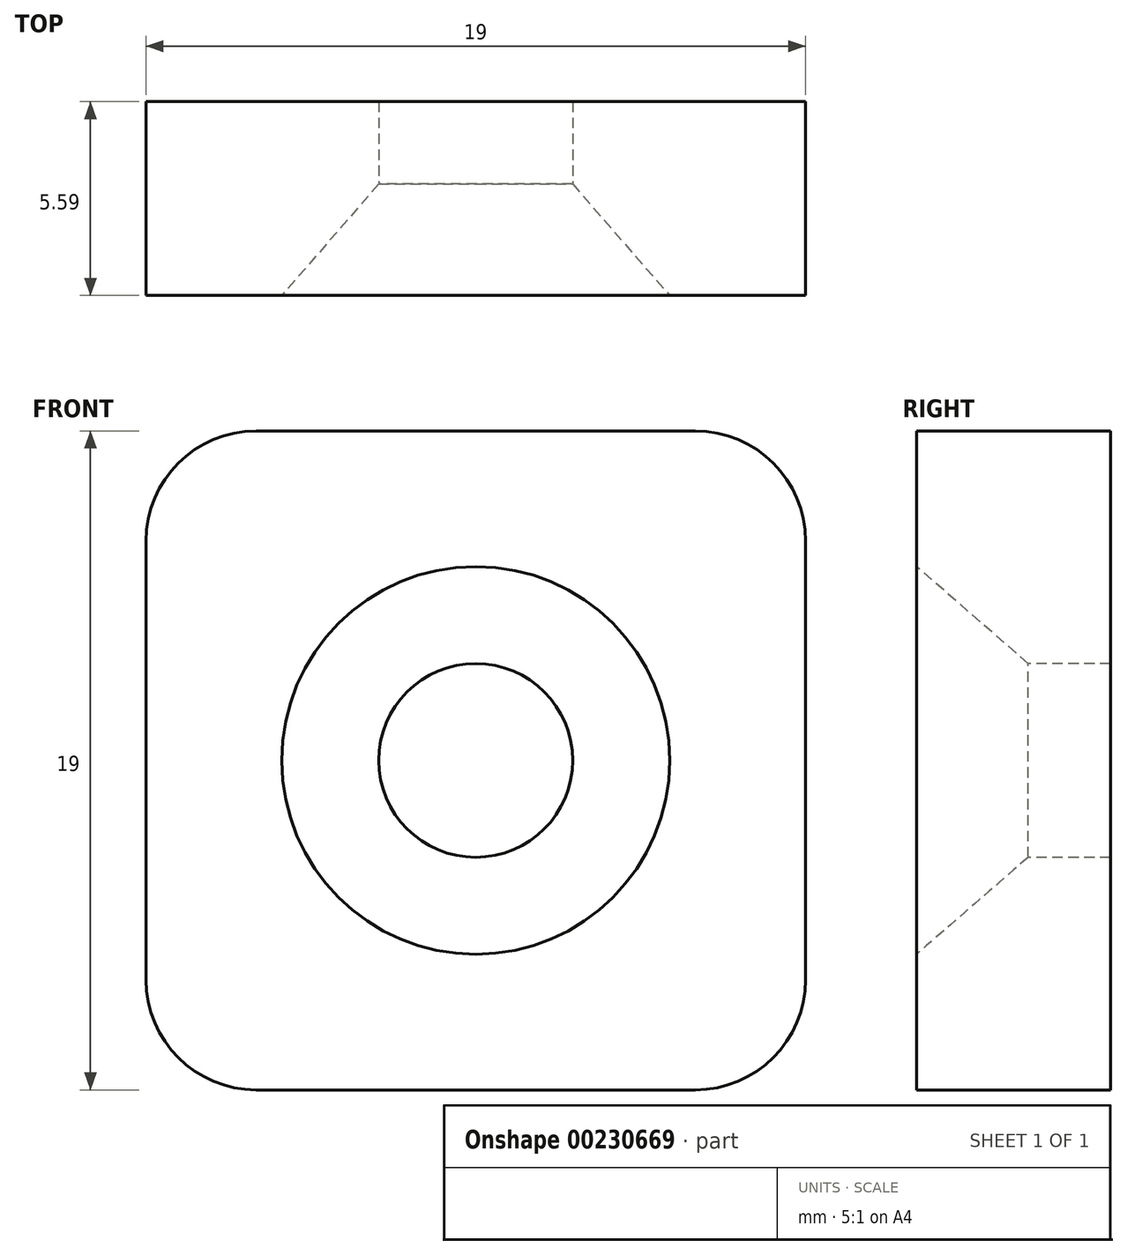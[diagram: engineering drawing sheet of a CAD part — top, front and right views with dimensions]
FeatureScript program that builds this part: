
annotation { "Feature Type Name" : "Feature", "Feature Type Description" : "" }
export const myFeature = defineFeature(function(context is Context, id is Id, definition is map)
    precondition{}
    {
        {
            var Q0;
            Q0=qCreatedBy(makeId("Front.planeOp"),FACE);
            var sketch = newSketch(context, id + "F0", { "sketchPlane" : qUnion([Q0])});
            skLineSegment(sketch, "E0.bottom", {"start": v(0, 0) * mm, "end": v(19, 0) * mm});
            skLineSegment(sketch, "E0.top", {"start": v(0, 19) * mm, "end": v(19, 19) * mm});
            skLineSegment(sketch, "E0.left", {"start": v(0, 0) * mm, "end": v(0, 19) * mm});
            skLineSegment(sketch, "E0.right", {"start": v(19, 0) * mm, "end": v(19, 19) * mm});
            skSolve(sketch);
        }
        {
            var Q0;
            Q0 = qSketchRegion(id + "F0", true);
            extrude(context, id + "F1", {"entities" : qUnion([Q0]), "depth" : 5.6 * mm});
        }
        {
            var Q0;
            Q0=makeQuery(id+"F1.opExtrude","SWEPT_EDGE",EDGE,{"disambiguationData":[OSD([sQuery(id+"F0.wireOp",EDGE,"E0.top"),sQuery(id+"F0.wireOp",EDGE,"E0.left")])]});
            var Q1;
            Q1=makeQuery(id+"F1.opExtrude","SWEPT_EDGE",EDGE,{"disambiguationData":[OSD([sQuery(id+"F0.wireOp",EDGE,"E0.top"),sQuery(id+"F0.wireOp",EDGE,"E0.right")])]});
            var Q2;
            Q2=makeQuery(id+"F1.opExtrude","SWEPT_EDGE",EDGE,{"disambiguationData":[OSD([sQuery(id+"F0.wireOp",EDGE,"E0.bottom"),sQuery(id+"F0.wireOp",EDGE,"E0.right")])]});
            var Q3;
            Q3=makeQuery(id+"F1.opExtrude","SWEPT_EDGE",EDGE,{"disambiguationData":[OSD([sQuery(id+"F0.wireOp",EDGE,"E0.bottom"),sQuery(id+"F0.wireOp",EDGE,"E0.left")])]});
            fillet(context, id + "F2", {"entities" : qUnion([Q0, Q1, Q2, Q3]), "radius" : 3.17 * mm, "tangentPropagation" : true, "allowEdgeOverflow" : false});
        }
        {
            var Q0;
            Q0=makeQuery(id+"F1.opExtrude","CAP_FACE",FACE,{"disambiguationData":[OSD([sQuery(id+"F0.wireOp",EDGE,"E0.bottom"),sQuery(id+"F0.wireOp",EDGE,"E0.top"),sQuery(id+"F0.wireOp",EDGE,"E0.left"),sQuery(id+"F0.wireOp",EDGE,"E0.right")])],"isStart":false});
            var sketch = newSketch(context, id + "F3", { "sketchPlane" : qUnion([Q0])});
            skLineSegment(sketch, "E1", {"start": v(9.5, 19) * mm, "end": v(9.5, 0) * mm});
            skPoint(sketch, "E2", {"position": v(9.5, 9.5) * mm});
            skSolve(sketch);
        }
        {
            var Q0;
            Q0=sQuery(id+"F3.wireOp",VERTEX,"E2");
            var Q1;
            Q1=makeQuery(id+"F1.opExtrude","SWEPT_BODY",BODY,{"disambiguationData":[OSD([sQuery(id+"F0.wireOp",EDGE,"E0.bottom"),sQuery(id+"F0.wireOp",EDGE,"E0.top"),sQuery(id+"F0.wireOp",EDGE,"E0.left"),sQuery(id+"F0.wireOp",EDGE,"E0.right")])]});
            hole(context, id + "F4", {"style" : HoleStyle.C_SINK, "endStyle" : HoleEndStyle.THROUGH, "holeDiameter" : 5.6 * mm, "cSinkDiameter" : 11.18 * mm, "cSinkAngle" : 82 * degree, "locations" : qUnion([Q0]), "scope" : qUnion([Q1]), "isTappedThrough" : true});
        }
    });
